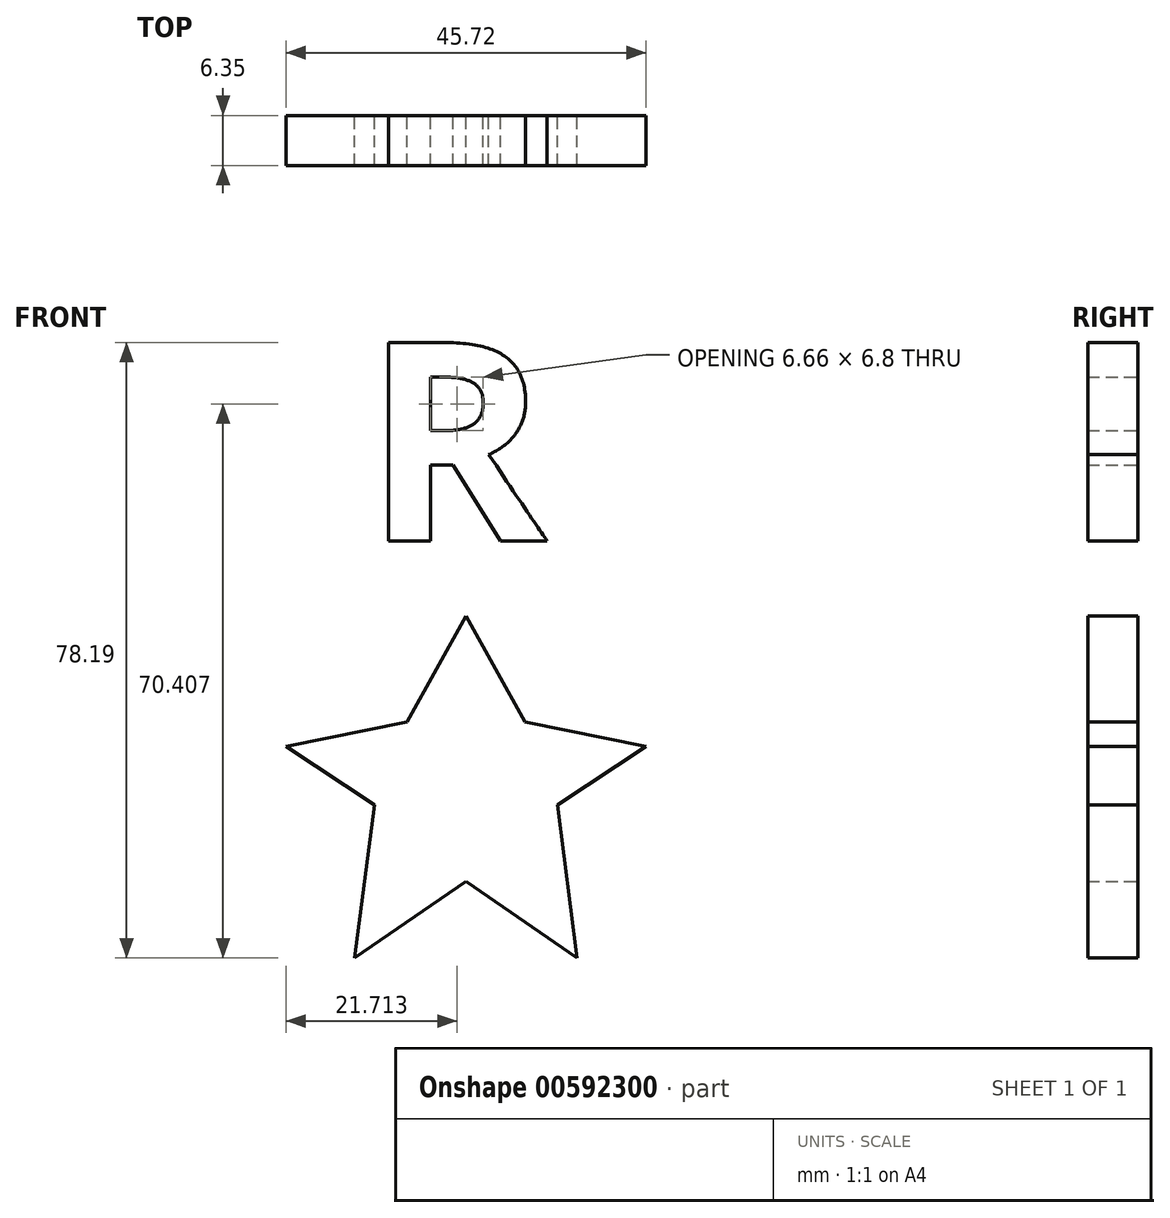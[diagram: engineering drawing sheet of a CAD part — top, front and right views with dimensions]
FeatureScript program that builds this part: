
annotation { "Feature Type Name" : "Feature", "Feature Type Description" : "" }
export const myFeature = defineFeature(function(context is Context, id is Id, definition is map)
    precondition{}
    {
        {
            var Q0;
            Q0=qCreatedBy(makeId("Front.planeOp"),FACE);
            var sketch = newSketch(context, id + "F0", { "sketchPlane" : qUnion([Q0])});
            skText(sketch, "E0", { "text": "R", "fontName": "OpenSans-Bold.ttf"});
            skLineSegment(sketch, "E1", {"start": v(-14.13, -19.45) * mm, "end": v(0, -9.73) * mm});
            skLineSegment(sketch, "E2.MirrorCS", {"start": v(14.13, -19.45) * mm, "end": v(0, -9.73) * mm});
            skLineSegment(sketch, "E3", {"start": v(-22.86, 7.43) * mm, "end": v(-11.61, 0) * mm});
            skLineSegment(sketch, "E4", {"start": v(-11.61, 0) * mm, "end": v(-14.13, -19.45) * mm});
            skLineSegment(sketch, "E5.MirrorCS", {"start": v(22.86, 7.43) * mm, "end": v(11.61, 0) * mm});
            skLineSegment(sketch, "E6.MirrorCS", {"start": v(11.61, 0) * mm, "end": v(14.13, -19.45) * mm});
            skPoint(sketch, "E7.4.start.orphan", {"position": v(22.86, 7.43) * mm});
            skPoint(sketch, "E8.orphan", {"position": v(14.13, -19.45) * mm});
            skLineSegment(sketch, "E9", {"start": v(-22.86, 7.43) * mm, "end": v(-7.48, 10.53) * mm});
            skLineSegment(sketch, "E10", {"start": v(-7.48, 10.53) * mm, "end": v(0, 24.04) * mm});
            skLineSegment(sketch, "E11.MirrorCS", {"start": v(7.48, 10.53) * mm, "end": v(0, 24.04) * mm});
            skLineSegment(sketch, "E12.MirrorCS", {"start": v(22.86, 7.43) * mm, "end": v(7.48, 10.53) * mm});
            const initialGuessF0  = {"E0": [-0.01299, 0.03355, 1, 0, 0.0254]};
            skSetInitialGuess(sketch, initialGuessF0);
            skSolve(sketch);
        }
        {
            var Q0;
            Q0=makeQuery(id+"F0.imprint","IMPRINT",FACE,{"disambiguationData":[TD([[makeQuery(id+"F0.imprint","IMPRINT",EDGE,{"derivedFrom":sQuery(id+"F0.wireOp",EDGE,"E0.sketch_text.stroke-0")}),-1.0]])]});
            var Q1;
            Q1=makeQuery(id+"F0.imprint","IMPRINT",FACE,{"disambiguationData":[TD([[makeQuery(id+"F0.imprint","IMPRINT",EDGE,{"derivedFrom":sQuery(id+"F0.wireOp",EDGE,"E1")}),1.0]])]});
            extrude(context, id + "F1", {"entities" : qUnion([Q0, Q1]), "depth" : 6.35 * mm, "offsetDistance" : 25.4 * mm});
        }
    });
